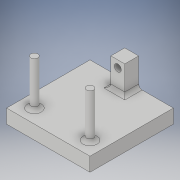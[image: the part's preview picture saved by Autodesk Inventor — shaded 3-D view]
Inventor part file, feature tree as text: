
AUTODESK INVENTOR PART (.ipt)
format: ipt  version: 2018 (Build 220112000, 112)  size: 154,624 bytes
history: native  units: in
note: dims shown in document units (in); Inventor stores cm internally (conversion verified against a paired STEP export)
features: sketch x6, extrude x3, hole x3, fillet x3
ambient origin geometry x8: Origin, YZ Plane, XZ Plane, XY Plane, X Axis, Y Axis, Z Axis, Center Point
bodies: Solid1 (feature_tree)
feature tree (15):
  extrude  "Extrusion1"  Depth=3.0in
  hole  "Hole1"  [1 undecoded]
  extrude  "Extrusion2"  Depth=1.0in TaperAngle=0.0deg
  hole  "Hole2"  [1 undecoded]
  fillet  "Fillet1"  Radius=1.625in
  hole  "Hole3"  [1 undecoded]
  extrude  "Extrusion3"  Depth=0.125in
  fillet  "Fillet2"  [1 undecoded]
  fillet  "Fillet3"  [1 undecoded]
  sketch  "Sketch1"  dims[d0=3.0in d1=3.0in]
  sketch  "Sketch2"  dims[d2=0.5in d3=0.0in]
  sketch  "Sketch3"  dims[d4=0.2in d5=0.75in d6=0.375in d7=0.25in d8=0.5635in d9=0.375in d10=0.8108in d11=0.5in]
  sketch  "Sketch4"  dims[d12=0.5in d13=1.0in d14=0.0in]
  sketch  "Sketch5"  dims[d15=0.25in d16=0.75in d17=0.375in d18=0.25in d19=0.5635in d20=0.5625in d21=0.8108in d22=0.125in]
  sketch  "Sketch6"  dims[d23=0.25in d24=0.75in d25=0.375in d26=0.25in d27=0.5635in d28=0.375in d29=0.8108in d30=1.625in d31=0.5005in d32=0.0in d33=0.0in d34=0.125in d35=0.125in]
note: 5 required parameter values undecoded (feature->parameter linkage not recoverable at this tier; creation-order binding heuristic only, values carry confidence <= 0.55)
